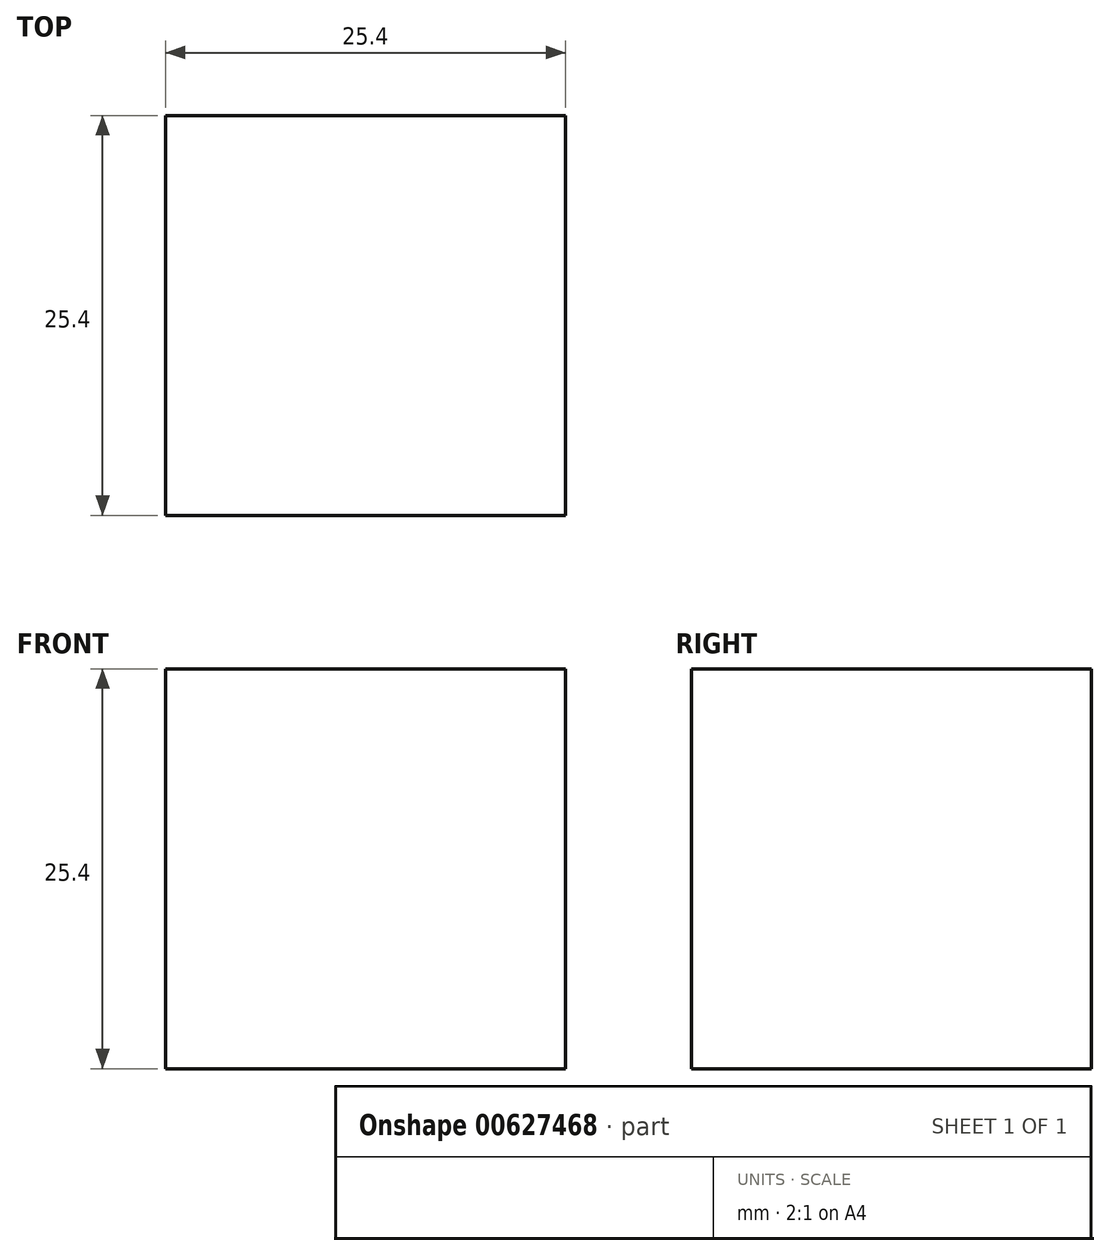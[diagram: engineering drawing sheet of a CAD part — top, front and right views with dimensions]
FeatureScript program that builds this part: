
annotation { "Feature Type Name" : "Feature", "Feature Type Description" : "" }
export const myFeature = defineFeature(function(context is Context, id is Id, definition is map)
    precondition{}
    {
        {
            var Q0;
            Q0=qCreatedBy(makeId("Front.planeOp"),FACE);
            var sketch = newSketch(context, id + "F0", { "sketchPlane" : qUnion([Q0])});
            skLineSegment(sketch, "E0.bottom", {"start": v(-25.4, 25.4) * mm, "end": v(0, 25.4) * mm});
            skLineSegment(sketch, "E0.top", {"start": v(-25.4, 0) * mm, "end": v(0, 0) * mm});
            skLineSegment(sketch, "E0.left", {"start": v(-25.4, 25.4) * mm, "end": v(-25.4, 0) * mm});
            skLineSegment(sketch, "E0.right", {"start": v(0, 25.4) * mm, "end": v(0, 0) * mm});
            skSolve(sketch);
        }
        {
            var Q0;
            Q0 = qSketchRegion(id + "F0", true);
            extrude(context, id + "F1", {"entities" : qUnion([Q0]), "depth" : 25.4 * mm, "offsetDistance" : 25.4 * mm});
        }
    });
